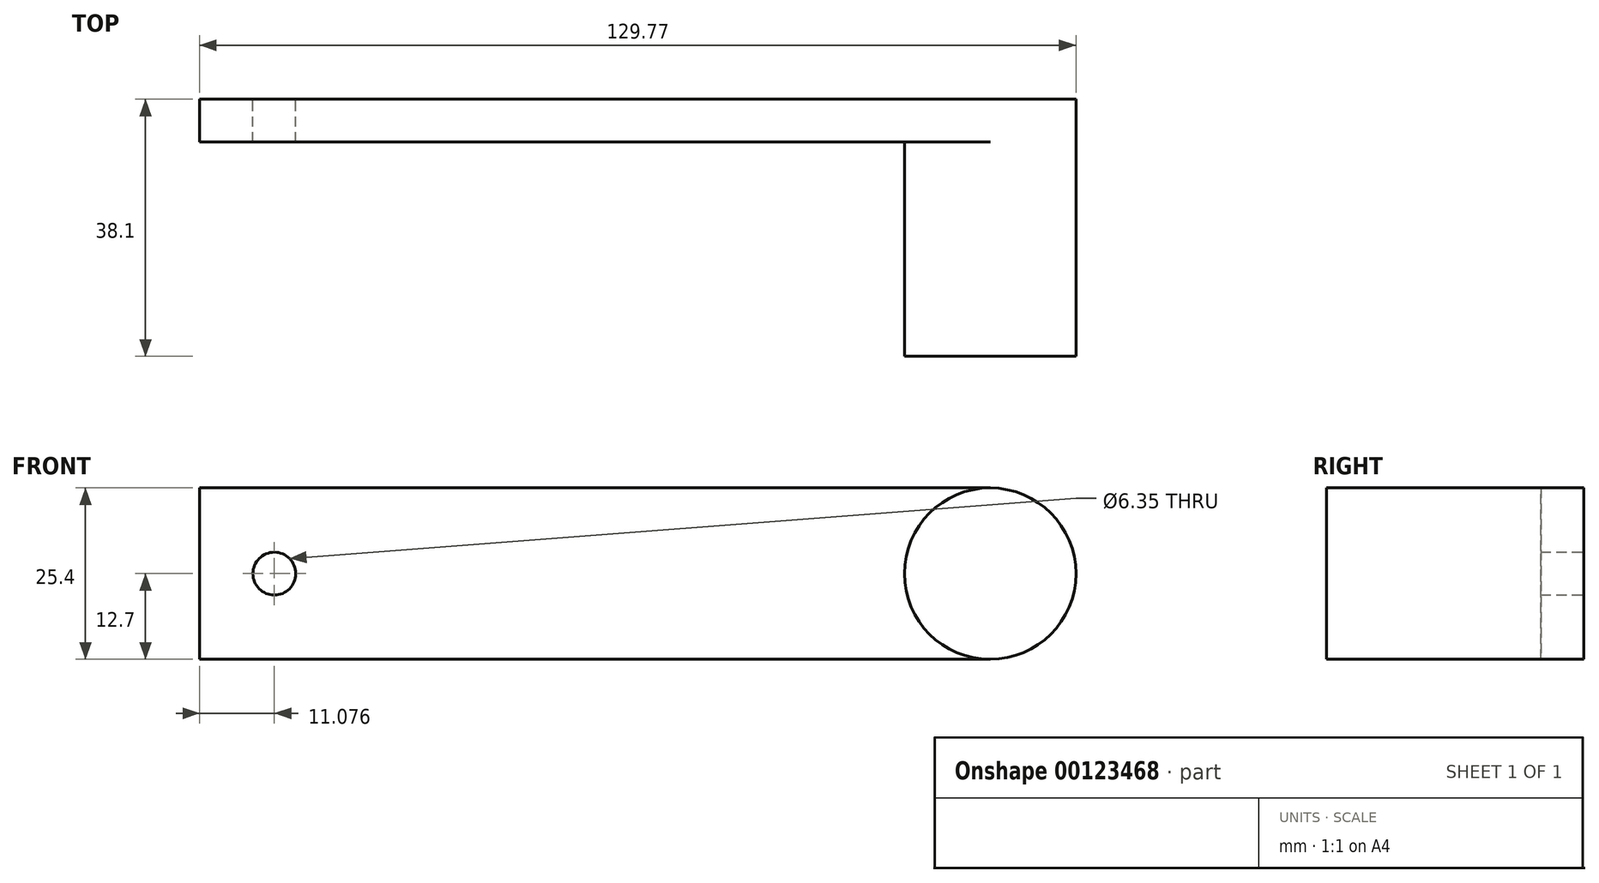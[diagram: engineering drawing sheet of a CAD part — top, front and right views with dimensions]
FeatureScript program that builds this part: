
annotation { "Feature Type Name" : "Feature", "Feature Type Description" : "" }
export const myFeature = defineFeature(function(context is Context, id is Id, definition is map)
    precondition{}
    {
        {
            var Q0;
            Q0=qCreatedBy(makeId("Front.planeOp"),FACE);
            var sketch = newSketch(context, id + "F0", { "sketchPlane" : qUnion([Q0])});
            skLineSegment(sketch, "E0.bottom", {"start": v(53.57, -12.7) * mm, "end": v(-63.5, -12.7) * mm});
            skLineSegment(sketch, "E0.top", {"start": v(53.57, 12.7) * mm, "end": v(-63.5, 12.7) * mm});
            skLineSegment(sketch, "E0.right", {"start": v(-63.5, -12.7) * mm, "end": v(-63.5, 12.7) * mm});
            skPoint(sketch, "E0.middle", {"position": v(0, 0) * mm});
            skPoint(sketch, "E1.centerSnap0", {"position": v(63.5, 0) * mm});
            skPoint(sketch, "E2.orphan", {"position": v(63.5, 12.7) * mm});
            skPoint(sketch, "E3.orphan", {"position": v(63.5, -12.7) * mm});
            skCircle(sketch, "E4", {"center": v(-52.42, 0) * mm, "radius": 3.18 * mm});
            skPoint(sketch, "E1.center.orphan", {"position": v(53.57, 0) * mm});
            skCircle(sketch, "E5", {"center": v(53.57, 0) * mm, "radius": 12.7 * mm});
            skSolve(sketch);
        }
        {
            var Q0;
            {var subQ1=sQuery(id+"F0.wireOp",EDGE,"E0.bottom");Q0=makeQuery(id+"F0.imprint","IMPRINT",FACE,{"disambiguationData":[TD([[makeQuery(id+"F0.imprint","IMPRINT",EDGE,{"derivedFrom":subQ1}),-1.0]])]});}
            extrude(context, id + "F1", {"entities" : qUnion([Q0]), "depth" : 6.35 * mm});
        }
        {
            var Q0;
            {var subQ0=sQuery(id+"F0.wireOp",EDGE,"E5");var subQ1=makeQuery(id+"F0.imprint","INTERSECT",VERTEX,{"derivedFrom":[sQuery(id+"F0.wireOp",EDGE,"E0.bottom"),subQ0]});Q0=makeQuery(id+"F0.imprint","IMPRINT",FACE,{"disambiguationData":[TD([[makeQuery(id+"F0.imprint","IMPRINT",EDGE,{"disambiguationData":[TD([[subQ1,1.0]])],"derivedFrom":subQ0}),1.0]])]});}
            extrude(context, id + "F2", {"entities" : qUnion([Q0]), "operationType" : NewBodyOperationType.ADD, "depth" : 38.1 * mm});
        }
    });
